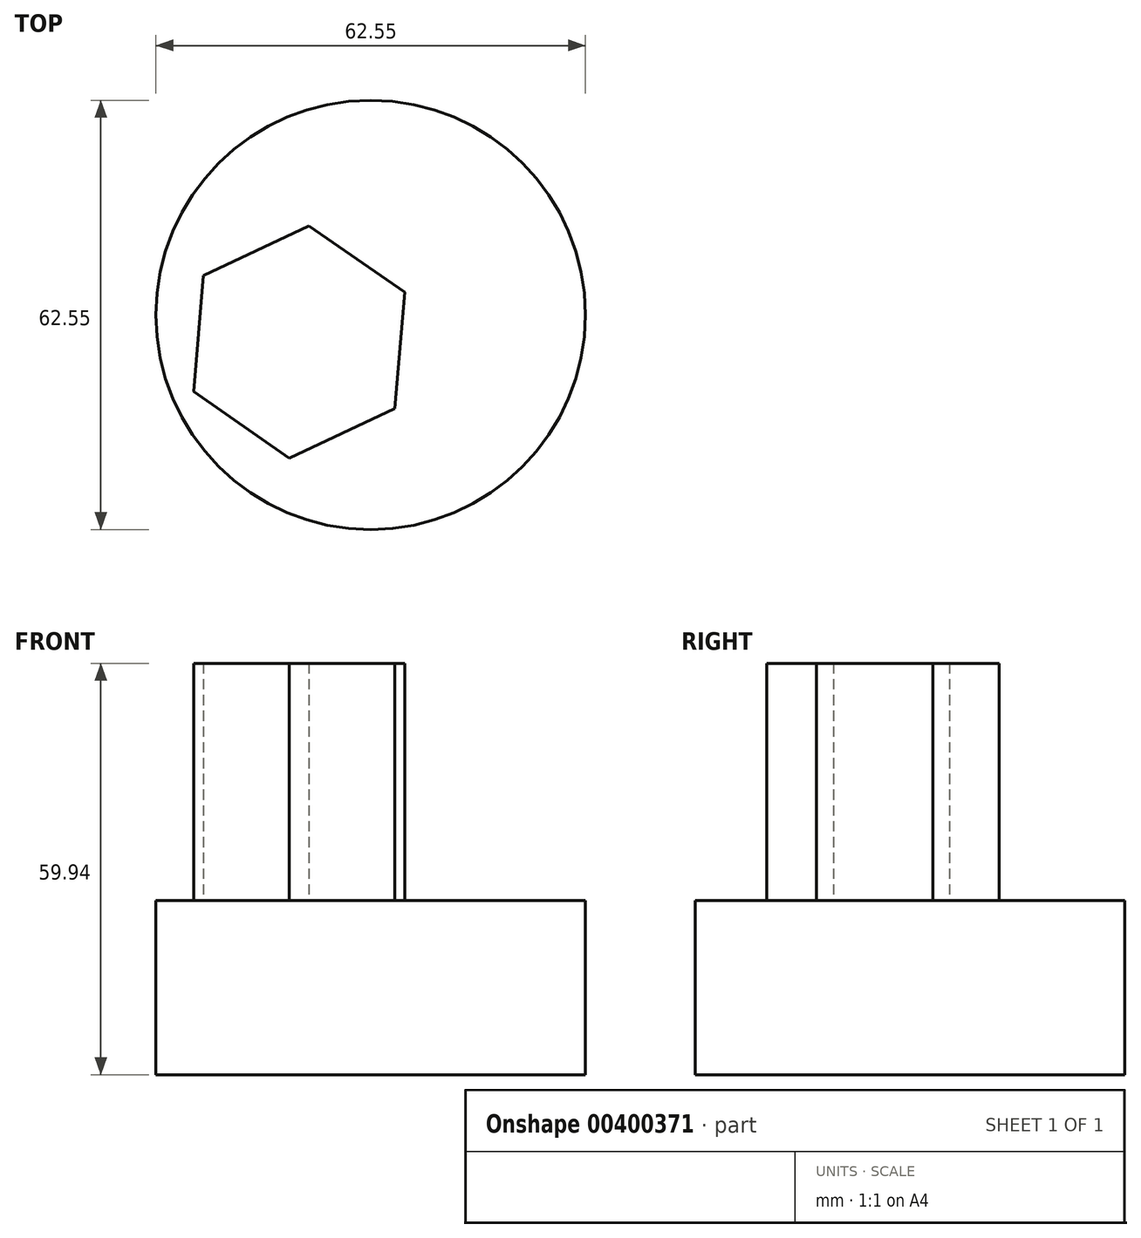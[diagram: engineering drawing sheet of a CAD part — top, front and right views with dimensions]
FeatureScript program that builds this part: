
annotation { "Feature Type Name" : "Feature", "Feature Type Description" : "" }
export const myFeature = defineFeature(function(context is Context, id is Id, definition is map)
    precondition{}
    {
        {
            var Q0;
            Q0=qCreatedBy(makeId("Top.planeOp"),FACE);
            var sketch = newSketch(context, id + "F0", { "sketchPlane" : qUnion([Q0])});
            skLineSegment(sketch, "E0.bottom", {"start": v(-70.77, -51.43) * mm, "end": v(54.08, -51.43) * mm});
            skLineSegment(sketch, "E0.top", {"start": v(-70.77, 65.06) * mm, "end": v(54.08, 65.06) * mm});
            skLineSegment(sketch, "E0.left", {"start": v(-70.77, -51.43) * mm, "end": v(-70.77, 65.06) * mm});
            skLineSegment(sketch, "E0.right", {"start": v(54.08, -51.43) * mm, "end": v(54.08, 65.06) * mm});
            skCircle(sketch, "E1", {"center": v(-51.37, 30.97) * mm, "radius": 31.27 * mm});
            skSolve(sketch);
        }
        {
            var Q0;
            {var subQ0=sQuery(id+"F0.wireOp",EDGE,"E1");var subQ1=sQuery(id+"F0.wireOp",EDGE,"E0.left");var subQ2=makeQuery(id+"F0.imprint","INTERSECT",VERTEX,{"disambiguationData":[OD(0.0)],"derivedFrom":[subQ1,subQ0]});Q0=makeQuery(id+"F0.imprint","IMPRINT",FACE,{"disambiguationData":[TD([[makeQuery(id+"F0.imprint","IMPRINT",EDGE,{"disambiguationData":[TD([[subQ2,-1.0]])],"derivedFrom":subQ1}),-1.0]])]});}
            var Q1;
            {var subQ0=sQuery(id+"F0.wireOp",EDGE,"E1");var subQ1=sQuery(id+"F0.wireOp",EDGE,"E0.left");var subQ2=makeQuery(id+"F0.imprint","INTERSECT",VERTEX,{"disambiguationData":[OD(0.0)],"derivedFrom":[subQ1,subQ0]});Q1=makeQuery(id+"F0.imprint","IMPRINT",FACE,{"disambiguationData":[TD([[makeQuery(id+"F0.imprint","IMPRINT",EDGE,{"disambiguationData":[TD([[subQ2,-1.0]])],"derivedFrom":subQ1}),1.0]])]});}
            extrude(context, id + "F1", {"entities" : qUnion([Q0, Q1]), "depth" : 25.4 * mm});
        }
        {
            var Q0;
            Q0=makeQuery(id+"F1.opExtrude","CAP_FACE",FACE,{"disambiguationData":[OSD([sQuery(id+"F0.wireOp",EDGE,"E1")])],"isStart":false});
            var sketch = newSketch(context, id + "F2", { "sketchPlane" : qUnion([Q0])});
            skCircle(sketch, "E2.cCircle", {"center": v(-61.78, 27.03) * mm, "radius": 14.7 * mm, "construction": true});
            skLineSegment(sketch, "E2.0", {"start": v(-47.84, 17.35) * mm, "end": v(-63.2, 10.11) * mm});
            skLineSegment(sketch, "E2.1", {"start": v(-63.2, 10.11) * mm, "end": v(-77.14, 19.8) * mm});
            skLineSegment(sketch, "E2.2", {"start": v(-77.14, 19.8) * mm, "end": v(-75.73, 36.71) * mm});
            skLineSegment(sketch, "E2.3", {"start": v(-75.73, 36.71) * mm, "end": v(-60.37, 43.95) * mm});
            skLineSegment(sketch, "E2.4", {"start": v(-60.37, 43.95) * mm, "end": v(-46.43, 34.27) * mm});
            skLineSegment(sketch, "E2.5", {"start": v(-46.43, 34.27) * mm, "end": v(-47.84, 17.35) * mm});
            skPoint(sketch, "E2.0.midPoint", {"position": v(-55.51, 13.73) * mm});
            skSolve(sketch);
        }
        {
            var Q0;
            Q0 = qSketchRegion(id + "F2", true);
            extrude(context, id + "F3", {"entities" : qUnion([Q0]), "operationType" : NewBodyOperationType.ADD, "depth" : 34.54 * mm});
        }
    });
